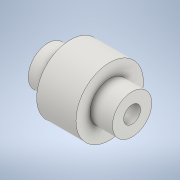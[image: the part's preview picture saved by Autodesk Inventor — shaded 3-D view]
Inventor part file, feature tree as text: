
AUTODESK INVENTOR PART (.ipt)
format: ipt  version: 2022 (Build 260153000, 153)  size: 117,760 bytes
history: native  units: mm
features: other x3, revolve x1, extrude x1, sketch x1
ambient origin geometry x6: Origin, XZ Plane, XY Plane, X Axis, Y Axis, Z Axis
bodies: Solid1 (feature_tree)
feature tree (6):
  revolve  "Revolution1"  [1 undecoded]
  extrude  "Extrusion1"  Depth=10.0mm
  other  "Start Plane"
  other  "Origin point"
  other  "Main Sketch"
  sketch  "Sketch3"  dims[d0=0.0mm d1=0.0mm d2=0.0mm d3=7.0mm d4=12.0mm d5=7.0mm d6=0.0mm d7=3.0mm d8=10.0mm d9=0.0mm]
note: 1 required parameter value undecoded (feature->parameter linkage not recoverable at this tier; creation-order binding heuristic only, values carry confidence <= 0.55)
